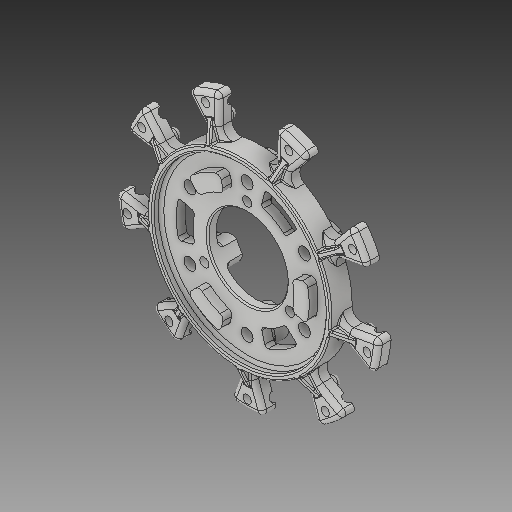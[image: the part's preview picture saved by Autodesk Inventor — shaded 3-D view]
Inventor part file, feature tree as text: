
AUTODESK INVENTOR PART (.ipt)
format: ipt  version: 2017 (Build 210142000, 142)  size: 2,275,328 bytes
history: native  units: in
note: dims shown in document units (in); Inventor stores cm internally (conversion verified against a paired STEP export)
features: fillet x1
ambient origin geometry x8: Origin, YZ Plane, XZ Plane, XY Plane, X Axis, Y Axis, Z Axis, Center Point
bodies: Solid1 (feature_tree)
feature tree (1):
  fillet  "Fillet19"  [1 undecoded]
note: 1 required parameter value undecoded (feature->parameter linkage not recoverable at this tier; creation-order binding heuristic only, values carry confidence <= 0.55)
